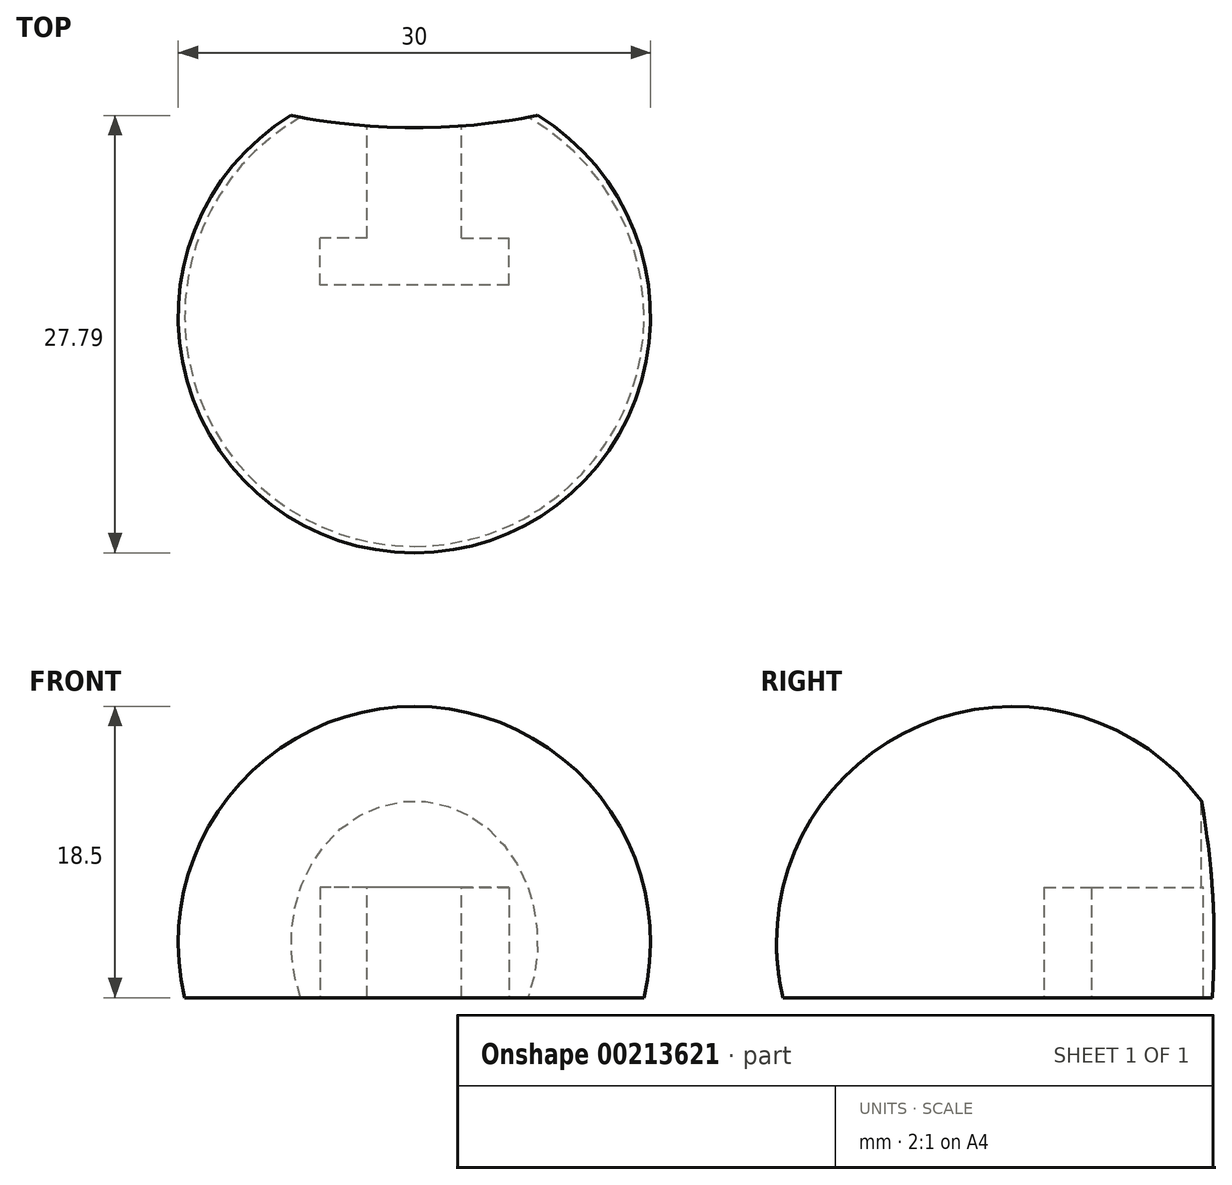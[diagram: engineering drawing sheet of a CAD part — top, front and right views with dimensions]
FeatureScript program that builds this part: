
annotation { "Feature Type Name" : "Feature", "Feature Type Description" : "" }
export const myFeature = defineFeature(function(context is Context, id is Id, definition is map)
    precondition{}
    {
        {
            var Q0;
            Q0=qCreatedBy(makeId("Right.planeOp"),FACE);
            var sketch = newSketch(context, id + "F0", { "sketchPlane" : qUnion([Q0])});
            skLineSegment(sketch, "E0", {"start": v(0, 0) * mm, "end": v(-30, 0) * mm});
            skArc(sketch, "E1", {"start": v(0, 0) * mm, "mid": v(-15, 15) * mm, "end": v(-30, 0) * mm});
            skSolve(sketch);
        }
        {
            var Q0;
            Q0=qSketchRegion(id+"F0",true);
            var Q1;
            Q1=sQuery(id+"F0.wireOp",EDGE,"E0");
            revolve(context, id + "F1", {"entities" : qUnion([Q0]), "axis" : qUnion([Q1]), "revolveType" : RevolveType.FULL});
        }
        {
            var Q0;
            Q0=qCreatedBy(makeId("Top.planeOp"),FACE);
            cPlane(context, id + "F2", {"entities" : qUnion([Q0]), "cplaneType" : CPlaneType.OFFSET, "offset" : 15 * mm, "width" : 150 * mm, "height" : 150 * mm});
        }
        {
            var Q0;
            Q0=qCreatedBy(id+"F2.planeOp",FACE);
            var sketch = newSketch(context, id + "F3", { "sketchPlane" : qUnion([Q0])});
            skLineSegment(sketch, "E2", {"start": v(0, 0) * mm, "end": v(0, -16.03) * mm, "construction": true});
            skLineSegment(sketch, "E3", {"start": v(0, 0) * mm, "end": v(-15, 0) * mm});
            skLineSegment(sketch, "E4", {"start": v(0, 0) * mm, "end": v(15, 0) * mm});
            skArc(sketch, "E5", {"start": v(-15, 0) * mm, "mid": v(0, -3) * mm, "end": v(15, 0) * mm});
            skSolve(sketch);
        }
        {
            var Q0;
            Q0=qSketchRegion(id+"F3",true);
            extrude(context, id + "F4", {"entities" : qUnion([Q0]), "operationType" : NewBodyOperationType.REMOVE, "endBound" : BoundingType.THROUGH_ALL, "oppositeDirection" : true, "depth" : 25 * mm});
        }
        {
            var Q0;
            Q0=qCreatedBy(makeId("Front.planeOp"),FACE);
            var sketch = newSketch(context, id + "F5", { "sketchPlane" : qUnion([Q0])});
            skLineSegment(sketch, "E6.bottom", {"start": v(3, -3.5) * mm, "end": v(-3, -3.5) * mm});
            skLineSegment(sketch, "E6.top", {"start": v(3, 3.5) * mm, "end": v(-3, 3.5) * mm});
            skLineSegment(sketch, "E6.left", {"start": v(3, -3.5) * mm, "end": v(3, 3.5) * mm});
            skLineSegment(sketch, "E6.right", {"start": v(-3, -3.5) * mm, "end": v(-3, 3.5) * mm});
            skPoint(sketch, "E6.middle", {"position": v(0, 0) * mm});
            skSolve(sketch);
        }
        {
            var Q0;
            Q0=qSketchRegion(id+"F5",true);
            extrude(context, id + "F6", {"entities" : qUnion([Q0]), "operationType" : NewBodyOperationType.REMOVE, "depth" : 13 * mm});
        }
        {
            var Q0;
            Q0=qCreatedBy(makeId("Front.planeOp"),FACE);
            var sketch = newSketch(context, id + "F7", { "sketchPlane" : qUnion([Q0])});
            skLineSegment(sketch, "E7.bottom", {"start": v(19.09, -3.5) * mm, "end": v(-19.09, -3.5) * mm});
            skLineSegment(sketch, "E7.top", {"start": v(19.09, -23.5) * mm, "end": v(-19.09, -23.5) * mm});
            skLineSegment(sketch, "E7.left", {"start": v(19.09, -3.5) * mm, "end": v(19.09, -23.5) * mm});
            skLineSegment(sketch, "E7.right", {"start": v(-19.09, -3.5) * mm, "end": v(-19.09, -23.5) * mm});
            skPoint(sketch, "E7.middle", {"position": v(0, -13.5) * mm});
            skSolve(sketch);
        }
        {
            var Q0;
            Q0 = qSketchRegion(id + "F7", true);
            extrude(context, id + "F8", {"entities" : qUnion([Q0]), "operationType" : NewBodyOperationType.REMOVE, "endBound" : BoundingType.THROUGH_ALL, "depth" : 25 * mm});
        }
        {
            var Q0;
            Q0=makeQuery(id+"F8.boolean.opBoolean","COPY",FACE,{"derivedFrom":makeQuery(id+"F8.opExtrude","SWEPT_FACE",FACE,{"disambiguationData":[OSD([sQuery(id+"F7.wireOp",EDGE,"E7.bottom")])]})});
            var sketch = newSketch(context, id + "F9", { "sketchPlane" : qUnion([Q0])});
            skLineSegment(sketch, "E8.bottom", {"start": v(-3, 13) * mm, "end": v(-6, 13) * mm});
            skLineSegment(sketch, "E8.top", {"start": v(-3, 10) * mm, "end": v(-6, 10) * mm});
            skLineSegment(sketch, "E8.left", {"start": v(-3, 13) * mm, "end": v(-3, 10) * mm});
            skLineSegment(sketch, "E8.right", {"start": v(-6, 13) * mm, "end": v(-6, 10) * mm});
            skLineSegment(sketch, "E9.bottom", {"start": v(3, 13) * mm, "end": v(6, 13) * mm});
            skLineSegment(sketch, "E9.top", {"start": v(3, 10) * mm, "end": v(6, 10) * mm});
            skLineSegment(sketch, "E9.left", {"start": v(3, 13) * mm, "end": v(3, 10) * mm});
            skLineSegment(sketch, "E9.right", {"start": v(6, 13) * mm, "end": v(6, 10) * mm});
            skSolve(sketch);
        }
        {
            var Q0;
            Q0 = qSketchRegion(id + "F9", true);
            extrude(context, id + "F10", {"entities" : qUnion([Q0]), "operationType" : NewBodyOperationType.REMOVE, "oppositeDirection" : true, "depth" : 7 * mm});
        }
        {
            var Q0;
            Q0 = qSketchRegion(id + "F7", true);
            extrude(context, id + "F11", {"entities" : qUnion([Q0]), "operationType" : NewBodyOperationType.REMOVE, "endBound" : BoundingType.THROUGH_ALL, "depth" : 25 * mm});
        }
    });
